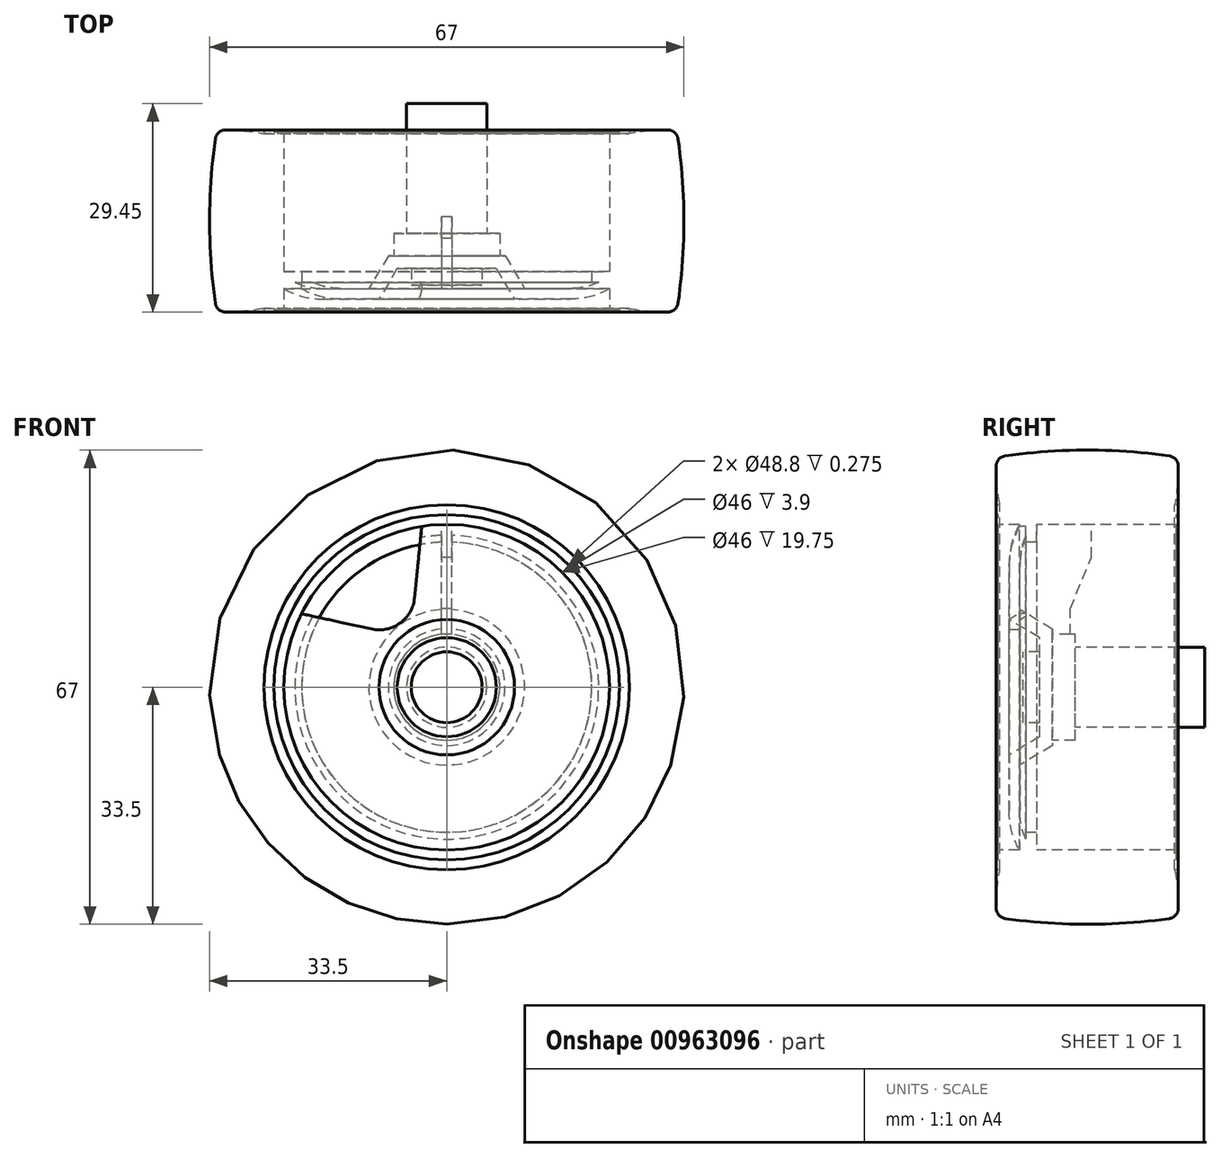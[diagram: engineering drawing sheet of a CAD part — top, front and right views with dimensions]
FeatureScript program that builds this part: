
annotation { "Feature Type Name" : "Feature", "Feature Type Description" : "" }
export const myFeature = defineFeature(function(context is Context, id is Id, definition is map)
    precondition{}
    {
        {
            var Q0;
            Q0=qCreatedBy(makeId("Right.planeOp"),FACE);
            var sketch = newSketch(context, id + "F0", { "sketchPlane" : qUnion([Q0])});
            skLineSegment(sketch, "E0", {"start": v(0, 0) * mm, "end": v(0, 5.67) * mm});
            skLineSegment(sketch, "E1", {"start": v(0, 5.67) * mm, "end": v(-18.3, 5.67) * mm});
            skLineSegment(sketch, "E2", {"start": v(-18.3, 5.67) * mm, "end": v(-18.3, 7.5) * mm});
            skLineSegment(sketch, "E3", {"start": v(-18.3, 7.5) * mm, "end": v(-21.5, 7.5) * mm});
            skLineSegment(sketch, "E4", {"start": v(-21.5, 7.5) * mm, "end": v(-21.5, 8.25) * mm});
            skLineSegment(sketch, "E5", {"start": v(-21.5, 8.25) * mm, "end": v(-26.11, 11) * mm});
            skLineSegment(sketch, "E6", {"start": v(-26.11, 11) * mm, "end": v(-26.11, 17.5) * mm});
            skArc(sketch, "E7", {"start": v(-25.25, 21.47) * mm, "mid": v(-25.9, 19.53) * mm, "end": v(-26.11, 17.5) * mm});
            skLineSegment(sketch, "E8", {"start": v(-25.25, 21.47) * mm, "end": v(-25.25, 20.5) * mm});
            skLineSegment(sketch, "E9", {"start": v(-25.25, 20.5) * mm, "end": v(-23.75, 20.5) * mm});
            skLineSegment(sketch, "E10", {"start": v(-23.75, 20.5) * mm, "end": v(-23.75, 23) * mm});
            skLineSegment(sketch, "E11", {"start": v(-23.75, 23) * mm, "end": v(-4, 23) * mm});
            skLineSegment(sketch, "E12", {"start": v(-4, 23) * mm, "end": v(-4, 24.4) * mm});
            skLineSegment(sketch, "E13", {"start": v(-4, 24.4) * mm, "end": v(-3.73, 24.4) * mm});
            skLineSegment(sketch, "E14", {"start": v(-3.73, 24.4) * mm, "end": v(-3.73, 25.8) * mm});
            skLineSegment(sketch, "E15", {"start": v(-3.73, 25.8) * mm, "end": v(-4.22, 25.8) * mm});
            skArc(sketch, "E16", {"start": v(-4.23, 25.8) * mm, "mid": v(-3.84, 28.49) * mm, "end": v(-3.7, 31.2) * mm});
            skArc(sketch, "E17", {"start": v(-5, 32.69) * mm, "mid": v(-16.58, 33.5) * mm, "end": v(-28.15, 32.69) * mm});
            skArc(sketch, "E18", {"start": v(-29.45, 31.2) * mm, "mid": v(-29.3, 28.49) * mm, "end": v(-28.93, 25.8) * mm});
            skLineSegment(sketch, "E19", {"start": v(-28.93, 25.8) * mm, "end": v(-29.43, 25.8) * mm});
            skLineSegment(sketch, "E20", {"start": v(-29.43, 25.8) * mm, "end": v(-29.43, 24.4) * mm});
            skLineSegment(sketch, "E21", {"start": v(-29.43, 24.4) * mm, "end": v(-29.15, 24.4) * mm});
            skLineSegment(sketch, "E22", {"start": v(-29.15, 24.4) * mm, "end": v(-29.15, 23) * mm});
            skLineSegment(sketch, "E23", {"start": v(-29.15, 23) * mm, "end": v(-26.15, 23) * mm});
            skArc(sketch, "E24", {"start": v(-26.15, 23) * mm, "mid": v(-27.24, 20.35) * mm, "end": v(-27.61, 17.5) * mm});
            skLineSegment(sketch, "E25", {"start": v(-27.61, 17.5) * mm, "end": v(-27.61, 9.57) * mm});
            skLineSegment(sketch, "E26", {"start": v(-27.61, 9.57) * mm, "end": v(-23.31, 7) * mm});
            skLineSegment(sketch, "E27", {"start": v(-23.31, 7) * mm, "end": v(-23.31, 5) * mm});
            skLineSegment(sketch, "E28", {"start": v(-23.31, 5) * mm, "end": v(-25.6, 5) * mm});
            skLineSegment(sketch, "E29", {"start": v(-25.6, 5) * mm, "end": v(-25.6, 0) * mm});
            skLineSegment(sketch, "E30", {"start": v(-25.6, 0) * mm, "end": v(0, 0) * mm});
            skPoint(sketch, "E31", {"position": v(-16.52, 33.5) * mm});
            skPoint(sketch, "E32.visualSharp", {"position": v(-3.73, 32.5) * mm});
            skArc(sketch, "E32.filletArc", {"start": v(-3.7, 31.2) * mm, "mid": v(-4.07, 32.18) * mm, "end": v(-5, 32.69) * mm});
            skPoint(sketch, "E33.visualSharp", {"position": v(-29.43, 32.5) * mm});
            skArc(sketch, "E33.filletArc", {"start": v(-28.15, 32.69) * mm, "mid": v(-29.08, 32.18) * mm, "end": v(-29.45, 31.2) * mm});
            skSolve(sketch);
        }
        {
            var Q0;
            Q0 = qSketchRegion(id + "F0", true);
            var Q1;
            Q1=sQuery(id+"F0.wireOp",EDGE,"E30");
            revolve(context, id + "F1", {"surfaceOperationType" : NewSurfaceOperationType.NEW, "entities" : qUnion([Q0]), "axis" : qUnion([Q1]), "revolveType" : RevolveType.FULL});
        }
        {
            var Q0;
            Q0=makeQuery(id+"F1.opRevolve","SWEPT_FACE",FACE,{"disambiguationData":[OSD([sQuery(id+"F0.wireOp",EDGE,"E22")])]});
            var sketch = newSketch(context, id + "F2", { "sketchPlane" : qUnion([Q0])});
            skArc(sketch, "E34", {"start": v(-3.53, 22.73) * mm, "mid": v(-13.52, 18.6) * mm, "end": v(-20.52, 10.38) * mm});
            skLineSegment(sketch, "E35", {"start": v(0, 0) * mm, "end": v(0, 28.38) * mm, "construction": true});
            skLineSegment(sketch, "E36", {"start": v(0, 0) * mm, "end": v(-27, 8.77) * mm, "construction": true});
            skLineSegment(sketch, "E37", {"start": v(0, 0) * mm, "end": v(-13.17, 18.12) * mm, "construction": true});
            skLineSegment(sketch, "E38", {"start": v(-20.52, 10.38) * mm, "end": v(-10.59, 8.22) * mm});
            skLineSegment(sketch, "E39", {"start": v(-4.55, 12.6) * mm, "end": v(-3.53, 22.73) * mm});
            skPoint(sketch, "E40.visualSharp", {"position": v(-5.1, 7.03) * mm});
            skArc(sketch, "E40.filletArc", {"start": v(-10.59, 8.22) * mm, "mid": v(-6.58, 9.06) * mm, "end": v(-4.55, 12.6) * mm});
            skPoint(sketch, "E41", {"position": v(-6.58, 9.06) * mm});
            skSolve(sketch);
        }
        {
            var Q0;
            Q0 = qSketchRegion(id + "F2", true);
            var Q1;
            Q1=makeQuery(id+"F1.opRevolve","SWEPT_FACE",FACE,{"disambiguationData":[OSD([sQuery(id+"F0.wireOp",EDGE,"E8")])]});
            extrude(context, id + "F3", {"entities" : qUnion([Q0]), "operationType" : NewBodyOperationType.REMOVE, "endBound" : BoundingType.UP_TO_SURFACE, "oppositeDirection" : true, "depth" : 25 * mm, "endBoundEntityFace" : qUnion([Q1]), "offsetDistance" : 25 * mm});
        }
        {
            var Q0;
            Q0=qCreatedBy(makeId("Right.planeOp"),FACE);
            var sketch = newSketch(context, id + "F4", { "sketchPlane" : qUnion([Q0])});
            skLineSegment(sketch, "E42", {"start": v(-19, 5.55) * mm, "end": v(-19, 11.07) * mm});
            skLineSegment(sketch, "E43", {"start": v(-19, 11.07) * mm, "end": v(-16, 18.32) * mm});
            skLineSegment(sketch, "E44", {"start": v(-16, 18.32) * mm, "end": v(-16, 25.17) * mm});
            skPoint(sketch, "E45.orphan", {"position": v(-4, 23) * mm});
            skPoint(sketch, "E46.orphan", {"position": v(-18.3, 7.5) * mm});
            skLineSegment(sketch, "E47", {"start": v(-19, 5.55) * mm, "end": v(-26.95, 10.75) * mm});
            skLineSegment(sketch, "E48", {"start": v(-26.95, 10.75) * mm, "end": v(-26.95, 19.28) * mm});
            skLineSegment(sketch, "E49", {"start": v(-26.95, 19.28) * mm, "end": v(-24.6, 25.03) * mm});
            skLineSegment(sketch, "E50", {"start": v(-24.6, 25.03) * mm, "end": v(-16, 25.17) * mm});
            skSolve(sketch);
        }
        {
            var Q0;
            Q0 = qSketchRegion(id + "F4", true);
            extrude(context, id + "F5", {"entities" : qUnion([Q0]), "operationType" : NewBodyOperationType.ADD, "depth" : 1.5 * mm, "offsetDistance" : 25 * mm, "symmetric" : true});
        }
    });
